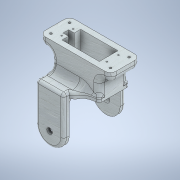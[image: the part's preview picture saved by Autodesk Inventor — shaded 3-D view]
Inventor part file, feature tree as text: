
AUTODESK INVENTOR PART (.ipt)
format: ipt  version: 2021 (Build 250183000, 183)  size: 643,072 bytes
history: native  units: mm
features: sketch x10, extrude x9, fillet x7, projected_geometry x2, plane x1
ambient origin geometry x8: Origin, YZ Plane, XZ Plane, XY Plane, X Axis, Y Axis, Z Axis, Center Point
bodies: Solid1 (feature_tree)
feature tree (29):
  extrude  "Extrusion1"  Depth=30.0mm
  extrude  "Extrusion2"  Depth=2.5mm TaperAngle=0.0deg
  plane  "Work Plane1"
  extrude  "Extrusion3"  Depth=3.5mm TaperAngle=0.0deg
  sketch  "Sketch4"  dims[d8=54.7mm d9=7.8mm d10=6.0mm d11=0.0mm]
  extrude  "Extrusion4"  Depth=7.8mm
  fillet  "Fillet1"  Radius=6.0mm
  extrude  "Extrusion5"  Depth=6.0mm
  extrude  "Extrusion6"  Depth=20.0mm
  extrude  "Extrusion7"  Depth=10.0mm
  fillet  "Fillet2"  Radius=6.0mm
  fillet  "Fillet3"  Radius=27.0mm
  fillet  "Fillet4"  Radius=27.0mm
  fillet  "Fillet5"  Radius=6.0mm
  fillet  "Fillet7"  Radius=7.0mm
  extrude  "Extrusion8"  Depth=10.0mm
  fillet  "Fillet8"  Radius=12.0mm
  extrude  "Extrusion9"  Depth=27.0mm TaperAngle=0.0deg
  sketch  "Sketch1"  dims[d0=20.6mm d1=30.0mm]
  sketch  "Sketch2"  dims[d2=35.0mm d3=2.5mm d4=0.0mm]
  projected_geometry  "Projected Loop1"
  sketch  "Sketch3"  dims[d5=6.0mm d6=3.5mm d7=0.0mm]
  projected_geometry  "Projected Loop2"
  sketch  "Sketch5"  dims[d12=6.0mm d13=0.0mm d14=6.0mm]
  sketch  "Sketch6"  dims[d15=40.0mm d16=20.0mm]
  sketch  "Sketch7"  dims[d17=10.0mm d18=10.0mm d19=6.0mm d20=27.0mm d21=0.0mm d22=27.0mm d23=0.0mm d24=6.0mm d25=7.0mm]
  sketch  "Sketch8"  dims[d26=12.0mm d27=10.0mm d28=12.0mm]
  sketch  "Sketch9"  dims[d29=10.0mm d30=27.0mm d31=0.0mm]
  sketch  "Sketch10"  dims[d32=6.0mm d33=6.0mm d34=3.0mm d35=3.0mm d37=6.0mm d38=2.4mm d39=2.4mm d40=2.4mm d41=2.4mm d42=12.0mm d43=0.0mm d44=8.0mm d45=10.0mm d46=0.0mm]
